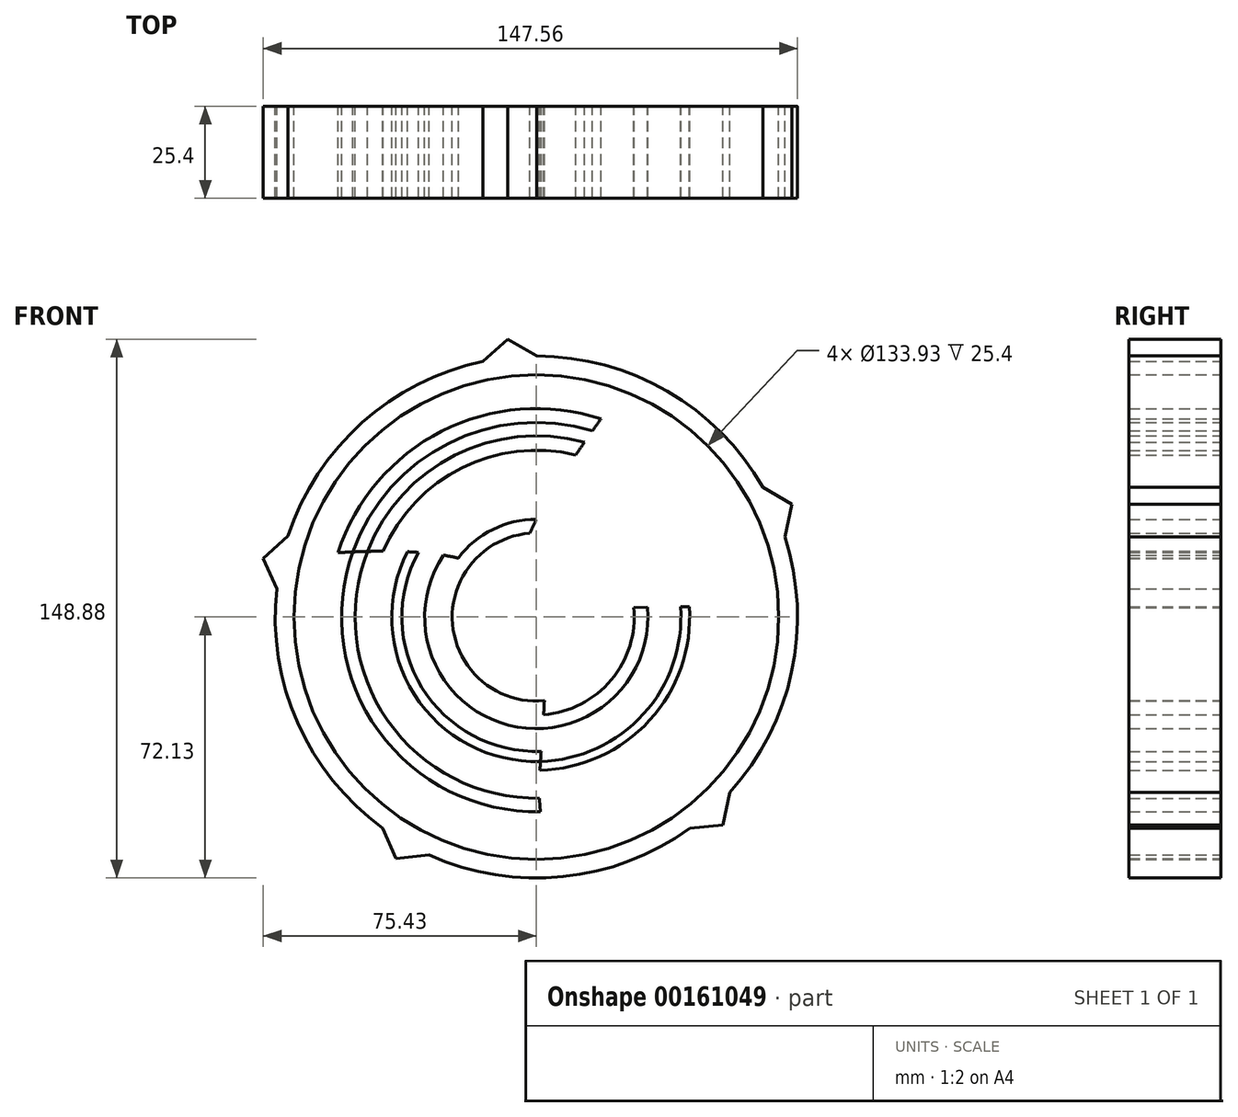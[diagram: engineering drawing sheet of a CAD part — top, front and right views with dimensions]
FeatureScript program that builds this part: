
annotation { "Feature Type Name" : "Feature", "Feature Type Description" : "" }
export const myFeature = defineFeature(function(context is Context, id is Id, definition is map)
    precondition{}
    {
        {
            var Q0;
            Q0=qCreatedBy(makeId("Front.planeOp"),FACE);
            var sketch = newSketch(context, id + "F0", { "sketchPlane" : qUnion([Q0])});
            skCircle(sketch, "E0.cCircle", {"center": v(0, 0) * mm, "radius": 62.42 * mm, "construction": true});
            skLineSegment(sketch, "E0.0", {"start": v(-7.88, 76.75) * mm, "end": v(70.56, 31.2) * mm});
            skLineSegment(sketch, "E0.1", {"start": v(70.56, 31.2) * mm, "end": v(51.49, -57.47) * mm});
            skLineSegment(sketch, "E0.2", {"start": v(51.49, -57.47) * mm, "end": v(-38.74, -66.72) * mm});
            skLineSegment(sketch, "E0.3", {"start": v(-38.74, -66.72) * mm, "end": v(-75.43, 16.23) * mm});
            skLineSegment(sketch, "E0.4", {"start": v(-75.43, 16.23) * mm, "end": v(-7.88, 76.75) * mm});
            skPoint(sketch, "E0.0.midPoint", {"position": v(31.34, 53.98) * mm});
            skFitSpline(sketch, "E1", {"points": [v(-75.43, 16.23) * mm, v(0, 0) * mm, v(6.37, -62.1) * mm, v(62.97, -4.1) * mm, v(0, 5.22) * mm, v(20.75, 58.87) * mm], "startDerivative": vector(473.98, 40.55) * mm, "endDerivative": vector(271.42, 381.64) * mm});
            skCircle(sketch, "E2", {"center": v(0, 0) * mm, "radius": 42.35 * mm});
            skCircle(sketch, "E3", {"center": v(0, 0) * mm, "radius": 30.84 * mm});
            skCircle(sketch, "E4", {"center": v(0, 0) * mm, "radius": 23.23 * mm});
            skCircle(sketch, "E5", {"center": v(0, 0) * mm, "radius": 19.94 * mm});
            skCircle(sketch, "E6", {"center": v(0, 0) * mm, "radius": 14.4 * mm});
            skCircle(sketch, "E7", {"center": v(0, 0) * mm, "radius": 9.96 * mm});
            skCircle(sketch, "E8", {"center": v(0, 0) * mm, "radius": 7.83 * mm});
            skCircle(sketch, "E9", {"center": v(0, 0) * mm, "radius": 6.1 * mm});
            skCircle(sketch, "E10", {"center": v(0, 0) * mm, "radius": 5.1 * mm});
            skCircle(sketch, "E11", {"center": v(0, 0) * mm, "radius": 3.32 * mm});
            skCircle(sketch, "E12", {"center": v(0, 0) * mm, "radius": 2.25 * mm});
            skCircle(sketch, "E13", {"center": v(0, 0) * mm, "radius": 57.62 * mm});
            skCircle(sketch, "E14", {"center": v(0, 0) * mm, "radius": 50.05 * mm});
            skCircle(sketch, "E15", {"center": v(0, 0) * mm, "radius": 37.13 * mm});
            skCircle(sketch, "E16", {"center": v(0, 0) * mm, "radius": 46.09 * mm});
            skCircle(sketch, "E17", {"center": v(0, 0) * mm, "radius": 53.79 * mm});
            skCircle(sketch, "E18", {"center": v(0, 0) * mm, "radius": 27.03 * mm});
            skCircle(sketch, "E19", {"center": v(0, 0) * mm, "radius": 33.79 * mm});
            skCircle(sketch, "E20", {"center": v(0, 0) * mm, "radius": 17.2 * mm});
            skCircle(sketch, "E21", {"center": v(0, 0) * mm, "radius": 12.43 * mm});
            skCircle(sketch, "E22", {"center": v(0, 0) * mm, "radius": 66.96 * mm});
            skCircle(sketch, "E23", {"center": v(0, 0) * mm, "radius": 72.13 * mm});
            skCircle(sketch, "E24", {"center": v(0, 0) * mm, "radius": 59.65 * mm});
            skCircle(sketch, "E25", {"center": v(0, 0) * mm, "radius": 39.93 * mm});
            skFitSpline(sketch, "E26.trimOffspring", {"points": [v(-75.43, 16.23) * mm, v(0, 0) * mm, v(6.37, -62.1) * mm, v(62.97, -4.1) * mm, v(0, 5.22) * mm, v(20.75, 58.87) * mm], "startDerivative": vector(473.98, 40.55) * mm, "endDerivative": vector(271.42, 381.64) * mm});
            skSolve(sketch);
        }
        {
            var Q0;
            Q0 = qSketchRegion(id + "F0", true);
            var Q1;
            {var subQ0=sQuery(id+"F0.wireOp",EDGE,"E3");var subQ1=sQuery(id+"F0.wireOp",EDGE,"E1");var subQ2=makeQuery(id+"F0.imprint","INTERSECT",VERTEX,{"disambiguationData":[OD(0.0)],"derivedFrom":[subQ1,subQ0]});Q1=makeQuery(id+"F0.imprint","IMPRINT",FACE,{"disambiguationData":[TD([[makeQuery(id+"F0.imprint","IMPRINT",EDGE,{"disambiguationData":[TD([[subQ2,-1.0]])],"derivedFrom":subQ1}),-1.0]])]});}
            var Q2;
            {var subQ0=sQuery(id+"F0.wireOp",EDGE,"E18");var subQ1=sQuery(id+"F0.wireOp",EDGE,"E1");var subQ2=makeQuery(id+"F0.imprint","INTERSECT",VERTEX,{"disambiguationData":[OD(0.0)],"derivedFrom":[subQ1,subQ0]});Q2=makeQuery(id+"F0.imprint","IMPRINT",FACE,{"disambiguationData":[TD([[makeQuery(id+"F0.imprint","IMPRINT",EDGE,{"disambiguationData":[TD([[subQ2,-1.0]])],"derivedFrom":subQ1}),-1.0]])]});}
            var Q3;
            {var subQ0=sQuery(id+"F0.wireOp",EDGE,"E25");var subQ1=sQuery(id+"F0.wireOp",EDGE,"E1");var subQ2=makeQuery(id+"F0.imprint","INTERSECT",VERTEX,{"disambiguationData":[OD(0.0)],"derivedFrom":[subQ1,subQ0]});Q3=makeQuery(id+"F0.imprint","IMPRINT",FACE,{"disambiguationData":[TD([[makeQuery(id+"F0.imprint","IMPRINT",EDGE,{"disambiguationData":[TD([[subQ2,-1.0]])],"derivedFrom":subQ1}),-1.0]])]});}
            var Q4;
            {var subQ0=sQuery(id+"F0.wireOp",EDGE,"E17");var subQ1=sQuery(id+"F0.wireOp",EDGE,"E1");var subQ2=makeQuery(id+"F0.imprint","INTERSECT",VERTEX,{"disambiguationData":[OD(0.0)],"derivedFrom":[subQ1,subQ0]});Q4=makeQuery(id+"F0.imprint","IMPRINT",FACE,{"disambiguationData":[TD([[makeQuery(id+"F0.imprint","IMPRINT",EDGE,{"disambiguationData":[TD([[subQ2,-1.0]])],"derivedFrom":subQ1}),-1.0]])]});}
            var Q5;
            {var subQ0=sQuery(id+"F0.wireOp",EDGE,"E18");var subQ1=sQuery(id+"F0.wireOp",EDGE,"E1");var subQ2=makeQuery(id+"F0.imprint","INTERSECT",VERTEX,{"disambiguationData":[OD(1.0)],"derivedFrom":[subQ1,subQ0]});Q5=makeQuery(id+"F0.imprint","IMPRINT",FACE,{"disambiguationData":[TD([[makeQuery(id+"F0.imprint","IMPRINT",EDGE,{"disambiguationData":[TD([[subQ2,-1.0]])],"derivedFrom":subQ1}),1.0]])]});}
            var Q6;
            {var subQ0=sQuery(id+"F0.wireOp",EDGE,"E18");var subQ1=sQuery(id+"F0.wireOp",EDGE,"E1");var subQ2=makeQuery(id+"F0.imprint","INTERSECT",VERTEX,{"disambiguationData":[OD(0.0)],"derivedFrom":[subQ1,subQ0]});Q6=makeQuery(id+"F0.imprint","IMPRINT",FACE,{"disambiguationData":[TD([[makeQuery(id+"F0.imprint","IMPRINT",EDGE,{"disambiguationData":[TD([[subQ2,-1.0]])],"derivedFrom":subQ1}),1.0]])]});}
            var Q7;
            {var subQ0=sQuery(id+"F0.wireOp",EDGE,"E2");var subQ1=sQuery(id+"F0.wireOp",EDGE,"E1");var subQ2=makeQuery(id+"F0.imprint","INTERSECT",VERTEX,{"disambiguationData":[OD(2.0)],"derivedFrom":[subQ1,subQ0]});Q7=makeQuery(id+"F0.imprint","IMPRINT",FACE,{"disambiguationData":[TD([[makeQuery(id+"F0.imprint","IMPRINT",EDGE,{"disambiguationData":[TD([[subQ2,-1.0]])],"derivedFrom":subQ1}),1.0]])]});}
            var Q8;
            {var subQ0=sQuery(id+"F0.wireOp",EDGE,"E25");var subQ1=sQuery(id+"F0.wireOp",EDGE,"E1");var subQ2=makeQuery(id+"F0.imprint","INTERSECT",VERTEX,{"disambiguationData":[OD(1.0)],"derivedFrom":[subQ1,subQ0]});Q8=makeQuery(id+"F0.imprint","IMPRINT",FACE,{"disambiguationData":[TD([[makeQuery(id+"F0.imprint","IMPRINT",EDGE,{"disambiguationData":[TD([[subQ2,-1.0]])],"derivedFrom":subQ1}),1.0]])]});}
            var Q9;
            {var subQ0=sQuery(id+"F0.wireOp",EDGE,"E13");var subQ2=sQuery(id+"F0.wireOp",EDGE,"E1");var subQ3=makeQuery(id+"F0.imprint","INTERSECT",VERTEX,{"disambiguationData":[OD(0.0)],"derivedFrom":[subQ2,subQ0]});Q9=makeQuery(id+"F0.imprint","IMPRINT",FACE,{"disambiguationData":[TD([[makeQuery(id+"F0.imprint","IMPRINT",EDGE,{"disambiguationData":[TD([[subQ3,-1.0]])],"derivedFrom":subQ2}),1.0]])]});}
            var Q10;
            {var subQ0=sQuery(id+"F0.wireOp",EDGE,"E14");var subQ1=sQuery(id+"F0.wireOp",EDGE,"E1");var subQ2=makeQuery(id+"F0.imprint","INTERSECT",VERTEX,{"disambiguationData":[OD(0.0)],"derivedFrom":[subQ1,subQ0]});Q10=makeQuery(id+"F0.imprint","IMPRINT",FACE,{"disambiguationData":[TD([[makeQuery(id+"F0.imprint","IMPRINT",EDGE,{"disambiguationData":[TD([[subQ2,-1.0]])],"derivedFrom":subQ1}),1.0]])]});}
            extrude(context, id + "F1", {"entities" : qUnion([Q0, Q1, Q2, Q3, Q4, Q5, Q6, Q7, Q8, Q9, Q10]), "depth" : 25.4 * mm});
        }
    });
